# Revit family: VP2A-45U-760x1200mm-14.03.14
name_source: partatom
category: Electrical Equipment
revit_build: Autodesk Revit 2013 (Build: 20120221_2030(x64)
units: mm (PartAtom-declared; Revit-internal decimal feet)

## types (1)
- VP2A-45U-760x1200mm-14.03.14
    Cabinet Depth = 1199.95 mm  [stored 3.93684 ft]
    Cabinet Height = 2145.65 mm  [stored 7.03953 ft]
    Cabinet Width Overall = 762 mm  [stored 2.5 ft]
    Color = BLACK
    Description = WARNING: PLEASE RELOAD FAMILY USING THE TYPE CATALOG
    Door Back = No
    Door Construction Side = 0
    Door Front = No
    Item Class = 1F
    Item Group = RACKS
    Manufacturer = SIEMON
    Model = VERSPOD
    Mounting Rail Material = SIEMON STEEL
    Ports = 0
    Rack Depth = 818 mm  [stored 2.68373 ft]
    Rack Width = 501 mm  [stored 1.6437 ft]
    Segment = CSS
    Side Panel Left = No
    Side Panel Right = No
    System = VPOD
    Top Frame Width = 578 mm  [stored 1.89633 ft]
    U Space = 45
    U/M = EA
    Weight = 0.00 lb

note: [stored X ft] marks values corroborated as IEEE doubles in the binary element streams (Revit-internal decimal feet)

## geometry (parser evidence)
native form markers: Blend x8, Sweep x7
no freeform markers — native parametric forms only
